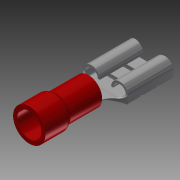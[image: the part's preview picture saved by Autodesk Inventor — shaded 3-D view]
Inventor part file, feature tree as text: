
AUTODESK INVENTOR PART (.ipt)
format: ipt  version: 2014 (Build 180170000, 170)  size: 540,672 bytes
history: native  units: in
note: dims shown in document units (in); Inventor stores cm internally (conversion verified against a paired STEP export)
features: sketch x13, extrude x10, projected_geometry x9, fillet x5, plane x3, shell x1, revolve x1, mirror x1, loft x1, chamfer x1
ambient origin geometry x8: Origin, YZ Plane, XZ Plane, XY Plane, X Axis, Y Axis, Z Axis, Center Point
bodies: Solid1 (feature_tree), Solid2 (feature_tree)
feature tree (45):
  extrude  "Extrusion1"  Depth=0.381in TaperAngle=0.0deg
  extrude  "Extrusion2"  Depth=0.03in TaperAngle=0.0deg
  fillet  "Fillet1"  Radius=0.02in
  fillet  "Fillet2"  Radius=0.03in
  shell  "Shell1"  Thickness=0.026in
  revolve  "Revolution1"  Angle=90.0deg
  plane  "Work Plane1"
  plane  "Work Plane2"
  extrude  "Extrusion3"  Depth=0.2905in
  mirror  "Mirror1"
  loft  "Loft2"
  fillet  "Fillet3"  Radius=0.109in
  chamfer  "Chamfer1"  Distance=0.291in
  extrude  "Extrusion4"  Depth=0.03in TaperAngle=45.0deg
  extrude  "Extrusion5"  Depth=0.3937in TaperAngle=90.0deg
  fillet  "Fillet4"  Radius=0.015in
  extrude  "Extrusion6"  Depth=0.015in TaperAngle=0.0deg
  extrude  "Extrusion7"  Depth=0.005in
  extrude  "Extrusion8"  Depth=0.003in TaperAngle=0.0deg
  fillet  "Fillet5"  Radius=0.003in
  plane  "Work Plane3"
  extrude  "Extrusion9"  Depth=0.005in
  extrude  "Extrusion10"  Depth=0.005in
  sketch  "Sketch1"  dims[d0=0.1755in d1=0.381in d2=0.0in]
  sketch  "Sketch2"  dims[d3=0.208in d4=0.16in d5=0.0in d6=0.02in d7=0.03in d8=0.026in]
  projected_geometry  "Projected Loop1"
  sketch  "Sketch3"  dims[d9=0.014in d10=90.0deg]
  sketch  "Sketch5"  dims[d11=0.4in d12=0.2905in]
  sketch  "Sketch6"  dims[d13=0.0135in d14=0.037in d15=0.109in]
  projected_geometry  "Projected Loop2"
  sketch  "Sketch7"  dims[d16=0.01in d17=0.291in d18=0.0in]
  projected_geometry  "Projected Loop3"
  sketch  "Sketch8"  dims[d23=0.03in d24=0.003in d25=0.125in d26=45.0deg]
  projected_geometry  "Projected Loop4"
  sketch  "Sketch9"  dims[d27=0.0in d28=90.0deg d29=0.3937in d30=90.0deg d31=0.015in]
  projected_geometry  "Projected Loop5"
  sketch  "Sketch10"  dims[d32=0.291in d33=0.0in d34=0.015in d35=0.0in]
  projected_geometry  "Projected Loop6"
  sketch  "Sketch11"  dims[d36=0.005in d37=0.0235in]
  projected_geometry  "Projected Loop7"
  sketch  "Sketch12"  dims[d38=0.014in d39=0.0in d40=0.003in d41=0.0in d42=0.003in d43=0.0in]
  sketch  "Sketch14"  dims[d44=0.005in d45=0.01in]
  sketch  "Sketch15"  dims[d46=0.003in d47=0.0in d48=0.005in d49=0.05in d50=0.0in]
  projected_geometry  "Projected Loop8"
  projected_geometry  "Project Cut Edges1"
